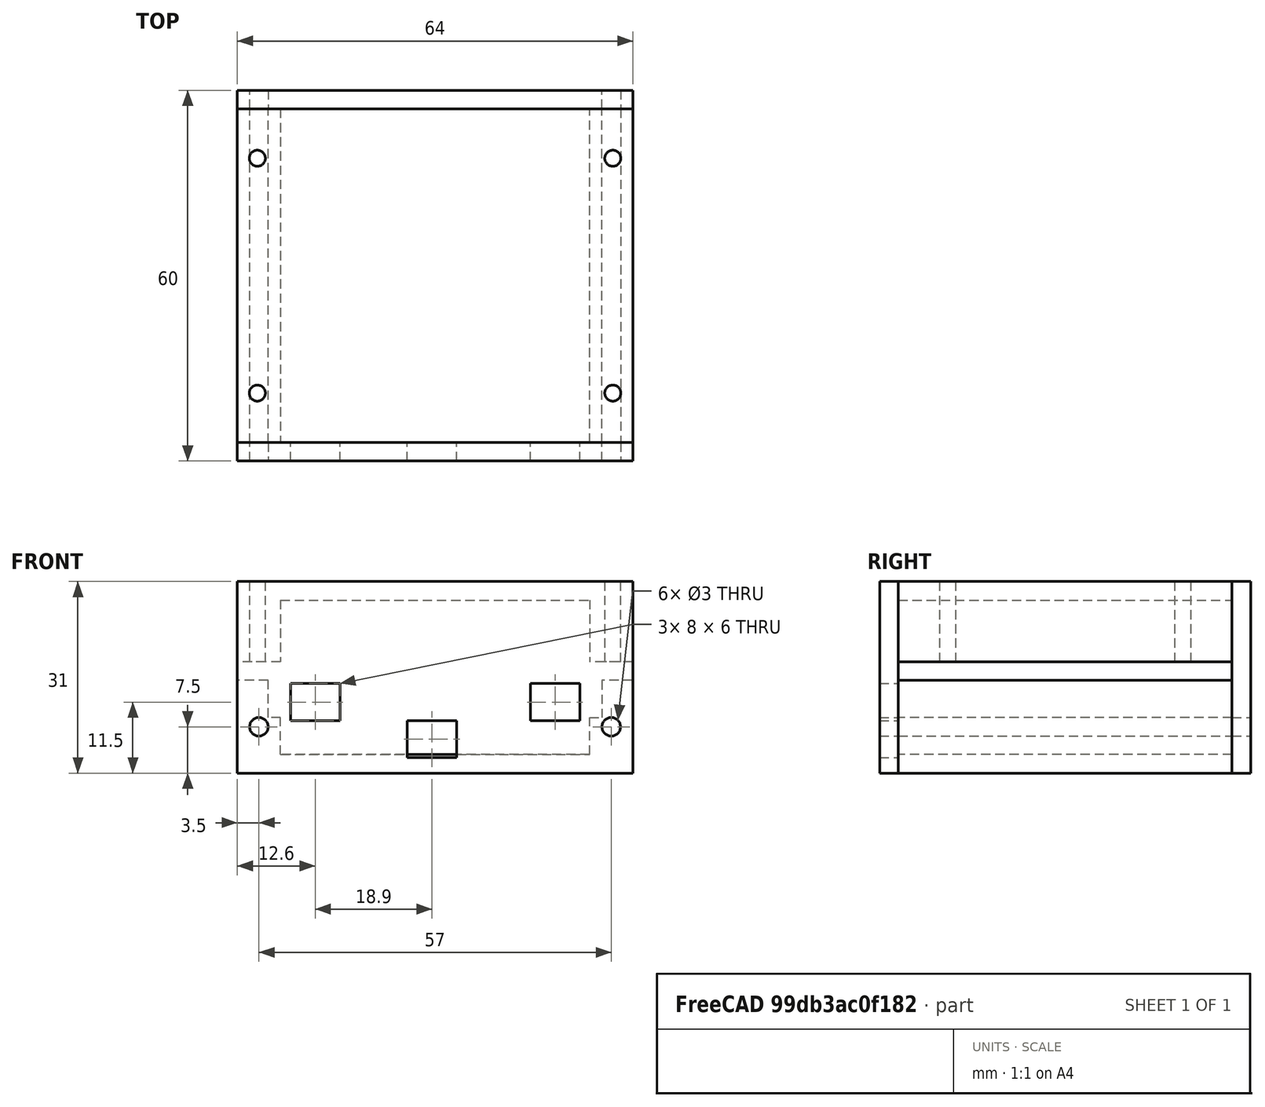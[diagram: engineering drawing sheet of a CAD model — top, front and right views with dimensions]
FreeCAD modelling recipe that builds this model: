
FCSTD DOCUMENT  (FreeCAD 0.20R29603 (Git))
Label: Remote Housing
License: All rights reserved
LicenseURL: http://en.wikipedia.org/wiki/All_rights_reserved
objects: Sketcher::SketchObject×16, PartDesign::Pocket×9, PartDesign::Pad×6, Mesh::Feature×5, PartDesign::Body×4
note: 50 computed .brp shape members not serialized (recipe doc carries the construction recipe); baked Part::Feature solids carry a one-line shape summary decoded from their .brp

FEATURE [Sketcher::SketchObject] Sketch
  FullyConstrained = true
  MapMode = 5
  Support = -> [XY_Plane]
  sketch-geometry (4):
    g0: LineSegment StartX=-32 StartY=27 StartZ=0 EndX=32 EndY=27 EndZ=0
    g1: LineSegment StartX=32 StartY=27 StartZ=0 EndX=32 EndY=-27 EndZ=0
    g2: LineSegment StartX=32 StartY=-27 StartZ=0 EndX=-32 EndY=-27 EndZ=0
    g3: LineSegment StartX=-32 StartY=-27 StartZ=0 EndX=-32 EndY=27 EndZ=0
  constraints (12):
    c: Horizontal(g0)
    c: Vertical(g1)
    c: Horizontal(g2)
    c: Vertical(g3)
    c: Coincident(g3,g0)
    c: Coincident(g0,g1)
    c: Coincident(g2,g1)
    c: Coincident(g2,g3)
    c: DistanceY(g1,g-1) = 27
    c: DistanceX(g-1,g0) = 32
    c: DistanceX(g0,g-1) = 32
    c: DistanceY(g-1,g0) = 27
FEATURE [Mesh::Feature] Holder
FEATURE [PartDesign::Pad] Pad
  Direction = (0,0,1)
  Length = 3
  Length2 = 10
  Profile = -> Sketch
  ReferenceAxis = -> Sketch [N_Axis]
  Type = 0
FEATURE [Mesh::Feature] Unnamed_Goouuu_ESP32_Development_Board001  label="ESP32_Development_Board"
  Placement = pos=(-3.3e-15,12,-3) rot=(-0.57735,-0.57735,0.57735;2.0944rad)
FEATURE [Mesh::Feature] Switch
  Placement = pos=(-10,-21,-9) rot=(0,0,1;3.14159rad)
FEATURE [Mesh::Feature] Switch001
  Placement = pos=(10,-21,-2.5) rot=(0,0,1;3.14159rad)
FEATURE [Mesh::Feature] Switch002
  Placement = pos=(-11,-21,-9) rot=(1,0,0;3.14159rad)
FEATURE [Sketcher::SketchObject] Sketch001  label="ThickWalls"
  FullyConstrained = true
  MapMode = 5
  Placement = pos=(0,0,0) rot=(1,0,0;3.14159rad)
  Support = -> [Pad]
  sketch-geometry (8):
    g0: LineSegment StartX=25 StartY=27 StartZ=0 EndX=32 EndY=27 EndZ=0
    g1: LineSegment StartX=32 StartY=27 StartZ=0 EndX=32 EndY=-27 EndZ=0
    g2: LineSegment StartX=32 StartY=-27 StartZ=0 EndX=25 EndY=-27 EndZ=0
    g3: LineSegment StartX=25 StartY=-27 StartZ=0 EndX=25 EndY=27 EndZ=0
    g4: LineSegment StartX=-32 StartY=27 StartZ=0 EndX=-25 EndY=27 EndZ=0
    g5: LineSegment StartX=-25 StartY=27 StartZ=0 EndX=-25 EndY=-27 EndZ=0
    g6: LineSegment StartX=-25 StartY=-27 StartZ=0 EndX=-32 EndY=-27 EndZ=0
    g7: LineSegment StartX=-32 StartY=-27 StartZ=0 EndX=-32 EndY=27 EndZ=0
  constraints (25):
    c: Horizontal(g0)
    c: Vertical(g1)
    c: Horizontal(g2)
    c: Vertical(g3)
    c: Coincident(g0,g3)
    c: Coincident(g0,g1)
    c: Coincident(g1,g2)
    c: Coincident(g2,g3)
    c: DistanceY(g-1,g0) = 27
    c: DistanceY(g1,g-1) = 27
    c: DistanceX(g-1,g0) = 25
    c: DistanceX(g0,g0) = 7
    c: Horizontal(g4)
    c: Vertical(g5)
    c: Horizontal(g6)
    c: PointOnObject(g7,g6)
    c: Vertical(g7)
    c: Coincident(g4,g7)
    c: Coincident(g4,g5)
    c: Coincident(g5,g6)
    c: DistanceX(g4,g-1) = 25
    c: DistanceX(g4,g4) = 7
    c: DistanceY(g-1,g4) = 27
    c: DistanceY(g7,g-1) = 27
    c: DistanceX(g6,g-1) = 32
FEATURE [PartDesign::Pad] Pad001
  BaseFeature = -> Pad
  Direction = (0,0,-1)
  Length = 10
  Length2 = 10
  Profile = -> Sketch001
  ReferenceAxis = -> Sketch001 [N_Axis]
  Type = 0
FEATURE [Sketcher::SketchObject] Sketch002  label="LeftHoles"
  FullyConstrained = true
  MapMode = 5
  Placement = pos=(0,0,-10) rot=(1,0,0;3.14159rad)
  Support = -> [Pad001]
  sketch-geometry (2):
    g0: Circle CenterX=-28.75 CenterY=19 CenterZ=0 NormalX=0 NormalY=0 NormalZ=1 AngleXU=0 Radius=1.3
    g1: Circle CenterX=-28.75 CenterY=-19 CenterZ=0 NormalX=0 NormalY=0 NormalZ=1 AngleXU=0 Radius=1.3
  constraints (6):
    c: DistanceY(g-1,g0) = 19
    c: DistanceY(g1,g-1) = 19
    c: Diameter(g0) = 2.6
    c: Diameter(g1) = 2.6
    c: DistanceX(g0,g-1) = 28.75
    c: DistanceX(g1,g-1) = 28.75
FEATURE [PartDesign::Pocket] Pocket
  BaseFeature = -> Pad001
  Direction = (0,0,1)
  Length = 20
  Length2 = 5
  Profile = -> Sketch002
  ReferenceAxis = -> Sketch002 [N_Axis]
  Type = 0
FEATURE [Sketcher::SketchObject] Sketch003  label="Right Holes"
  FullyConstrained = true
  MapMode = 5
  Placement = pos=(0,0,-10) rot=(1,0,0;3.14159rad)
  Support = -> [Pocket]
  sketch-geometry (2):
    g0: Circle CenterX=28.75 CenterY=19 CenterZ=0 NormalX=0 NormalY=0 NormalZ=1 AngleXU=0 Radius=1.3
    g1: Circle CenterX=28.75 CenterY=-19 CenterZ=0 NormalX=0 NormalY=0 NormalZ=1 AngleXU=0 Radius=1.3
  constraints (6):
    c: DistanceY(g-1,g0) = 19
    c: DistanceX(g-1,g0) = 28.75
    c: Diameter(g0) = 2.6
    c: DistanceX(g-1,g1) = 28.75
    c: DistanceY(g1,g-1) = 19
    c: Diameter(g1) = 2.6
FEATURE [PartDesign::Pocket] Pocket001
  BaseFeature = -> Pocket
  Direction = (0,0,1)
  Length = 20
  Length2 = 5
  Profile = -> Sketch003
  ReferenceAxis = -> Sketch003 [N_Axis]
  Type = 0
FEATURE [PartDesign::Body] Body  label="Battery Cover Bottom"
  Group = -> [Sketch,Pad,Sketch001,Pad001,Sketch002,Pocket,Sketch003,Pocket001]
  Origin = -> Origin
  Placement = pos=(0,0,10.5) rot=(0,0,1;0rad)
  Tip = -> Pocket001
FEATURE [Sketcher::SketchObject] Sketch004
  FullyConstrained = true
  MapMode = 5
  Support = -> [XY_Plane001]
  sketch-geometry (4):
    g0: LineSegment StartX=-32 StartY=27 StartZ=0 EndX=32 EndY=27 EndZ=0
    g1: LineSegment StartX=32 StartY=27 StartZ=0 EndX=32 EndY=-27 EndZ=0
    g2: LineSegment StartX=32 StartY=-27 StartZ=0 EndX=-32 EndY=-27 EndZ=0
    g3: LineSegment StartX=-32 StartY=-27 StartZ=0 EndX=-32 EndY=27 EndZ=0
  constraints (12):
    c: Horizontal(g0)
    c: Vertical(g1)
    c: Horizontal(g2)
    c: Vertical(g3)
    c: Coincident(g3,g0)
    c: Coincident(g0,g1)
    c: Coincident(g2,g1)
    c: Coincident(g2,g3)
    c: DistanceY(g1,g-1) = 27
    c: DistanceX(g-1,g0) = 32
    c: DistanceX(g0,g-1) = 32
    c: DistanceY(g-1,g0) = 27
FEATURE [PartDesign::Pad] Pad002
  Direction = (0,0,1)
  Length = 3
  Length2 = 10
  Profile = -> Sketch004
  ReferenceAxis = -> Sketch004 [N_Axis]
  Type = 0
FEATURE [Sketcher::SketchObject] Sketch005  label="ThickWalls001"
  FullyConstrained = true
  MapMode = 5
  Placement = pos=(0,0,0) rot=(1,0,0;3.14159rad)
  Support = -> [Pad002]
  sketch-geometry (8):
    g0: LineSegment StartX=25 StartY=27 StartZ=0 EndX=32 EndY=27 EndZ=0
    g1: LineSegment StartX=32 StartY=27 StartZ=0 EndX=32 EndY=-27 EndZ=0
    g2: LineSegment StartX=32 StartY=-27 StartZ=0 EndX=25 EndY=-27 EndZ=0
    g3: LineSegment StartX=25 StartY=-27 StartZ=0 EndX=25 EndY=27 EndZ=0
    g4: LineSegment StartX=-32 StartY=27 StartZ=0 EndX=-25 EndY=27 EndZ=0
    g5: LineSegment StartX=-25 StartY=27 StartZ=0 EndX=-25 EndY=-27 EndZ=0
    g6: LineSegment StartX=-25 StartY=-27 StartZ=0 EndX=-32 EndY=-27 EndZ=0
    g7: LineSegment StartX=-32 StartY=-27 StartZ=0 EndX=-32 EndY=27 EndZ=0
  constraints (25):
    c: Horizontal(g0)
    c: Vertical(g1)
    c: Horizontal(g2)
    c: Vertical(g3)
    c: Coincident(g0,g3)
    c: Coincident(g0,g1)
    c: Coincident(g1,g2)
    c: Coincident(g2,g3)
    c: DistanceY(g-1,g0) = 27
    c: DistanceY(g1,g-1) = 27
    c: DistanceX(g-1,g0) = 25
    c: DistanceX(g0,g0) = 7
    c: Horizontal(g4)
    c: Vertical(g5)
    c: Horizontal(g6)
    c: PointOnObject(g7,g6)
    c: Vertical(g7)
    c: Coincident(g4,g7)
    c: Coincident(g4,g5)
    c: Coincident(g5,g6)
    c: DistanceX(g4,g-1) = 25
    c: DistanceX(g4,g4) = 7
    c: DistanceY(g-1,g4) = 27
    c: DistanceY(g7,g-1) = 27
    c: DistanceX(g6,g-1) = 32
FEATURE [PartDesign::Pad] Pad003
  BaseFeature = -> Pad002
  Direction = (0,0,-1)
  Length = 12
  Length2 = 10
  Profile = -> Sketch005
  ReferenceAxis = -> Sketch005 [N_Axis]
  Type = 0
FEATURE [Sketcher::SketchObject] Sketch008  label="Right"
  FullyConstrained = true
  MapMode = 5
  Placement = pos=(0,-27,0) rot=(1,0,0;1.5708rad)
  Support = -> [Pad003]
  sketch-geometry (1):
    g0: Circle CenterX=28.5 CenterY=-4.5 CenterZ=0 NormalX=0 NormalY=0 NormalZ=1 AngleXU=0 Radius=1.5
  constraints (3):
    c: DistanceX(g-1,g0) = 28.5
    c: Diameter(g0) = 3
    c: DistanceY(g0,g-1) = 4.5
FEATURE [PartDesign::Pocket] Pocket003
  BaseFeature = -> Pad003
  Direction = (0,1,-2e-16)
  Length = 60
  Length2 = 5
  Profile = -> Sketch008
  ReferenceAxis = -> Sketch008 [N_Axis]
  Type = 0
FEATURE [Sketcher::SketchObject] Sketch009  label="Left"
  FullyConstrained = true
  MapMode = 5
  Placement = pos=(0,-27,0) rot=(1,0,0;1.5708rad)
  Support = -> [Pocket003]
  sketch-geometry (1):
    g0: Circle CenterX=-28.5 CenterY=-4.5 CenterZ=0 NormalX=0 NormalY=0 NormalZ=1 AngleXU=0 Radius=1.5
  constraints (3):
    c: Diameter(g0) = 3
    c: DistanceY(g0,g-1) = 4.5
    c: DistanceX(g0,g-1) = 28.5
FEATURE [PartDesign::Pocket] Pocket004
  BaseFeature = -> Pocket003
  Direction = (0,1,-2e-16)
  Length = 60
  Length2 = 5
  Profile = -> Sketch009
  ReferenceAxis = -> Sketch009 [N_Axis]
  Type = 0
FEATURE [Sketcher::SketchObject] Sketch010  label="Side 01"
  FullyConstrained = true
  Placement = pos=(0,30,0) rot=(1,0,0;1.5708rad)
  sketch-geometry (4):
    g0: LineSegment StartX=-32 StartY=13.5 StartZ=0 EndX=32 EndY=13.5 EndZ=0
    g1: LineSegment StartX=32 StartY=13.5 StartZ=0 EndX=32 EndY=-17.5 EndZ=0
    g2: LineSegment StartX=32 StartY=-17.5 StartZ=0 EndX=-32 EndY=-17.5 EndZ=0
    g3: LineSegment StartX=-32 StartY=-17.5 StartZ=0 EndX=-32 EndY=13.5 EndZ=0
  constraints (12):
    c: Horizontal(g0)
    c: Vertical(g1)
    c: Horizontal(g2)
    c: Vertical(g3)
    c: Coincident(g3,g0)
    c: Coincident(g1,g0)
    c: Coincident(g2,g1)
    c: Coincident(g2,g3)
    c: DistanceY(g-1,g0) = 13.5
    c: DistanceX(g0,g-1) = 32
    c: DistanceX(g-1,g0) = 32
    c: DistanceY(g2,g-1) = 17.5
FEATURE [PartDesign::Pad] Pad005
  Direction = (0,-1,2e-16)
  Length = 3
  Length2 = 10
  Placement = pos=(0,30,0) rot=(1,0,0;1.5708rad)
  Profile = -> Sketch010
  ReferenceAxis = -> Sketch010 [N_Axis]
  Type = 0
FEATURE [Sketcher::SketchObject] Sketch011  label="SideHoles"
  FullyConstrained = true
  MapMode = 5
  Placement = pos=(0,30,0) rot=(-1,0,0;1.5708rad)
  Support = -> [Pad005]
  sketch-geometry (2):
    g0: Circle CenterX=28.5 CenterY=10 CenterZ=0 NormalX=0 NormalY=0 NormalZ=1 AngleXU=0 Radius=1.5
    g1: Circle CenterX=-28.5 CenterY=10 CenterZ=0 NormalX=0 NormalY=0 NormalZ=1 AngleXU=0 Radius=1.5
  constraints (6):
    c: Diameter(g0) = 3
    c: Diameter(g1) = 3
    c: DistanceY(g-1,g1) = 10
    c: DistanceY(g-1,g0) = 10
    c: DistanceX(g-1,g0) = 28.5
    c: DistanceX(g1,g-1) = 28.5
FEATURE [PartDesign::Pocket] Pocket005
  BaseFeature = -> Pad005
  Direction = (0,-1,2e-16)
  Length = 5
  Length2 = 5
  Placement = pos=(0,30,0) rot=(1,0,0;1.5708rad)
  Profile = -> Sketch011
  ReferenceAxis = -> Sketch011 [N_Axis]
  Type = 0
FEATURE [PartDesign::Body] Body003  label="Side1"
  Group = -> [Sketch010,Pad005,Sketch011,Pocket005]
  Origin = -> Origin003
  Tip = -> Pocket005
FEATURE [Sketcher::SketchObject] Sketch012  label="Side 002"
  FullyConstrained = true
  Placement = pos=(0,30,0) rot=(1,0,0;1.5708rad)
  sketch-geometry (4):
    g0: LineSegment StartX=-32 StartY=13.5 StartZ=0 EndX=32 EndY=13.5 EndZ=0
    g1: LineSegment StartX=32 StartY=13.5 StartZ=0 EndX=32 EndY=-17.5 EndZ=0
    g2: LineSegment StartX=32 StartY=-17.5 StartZ=0 EndX=-32 EndY=-17.5 EndZ=0
    g3: LineSegment StartX=-32 StartY=-17.5 StartZ=0 EndX=-32 EndY=13.5 EndZ=0
  constraints (12):
    c: Horizontal(g0)
    c: Vertical(g1)
    c: Horizontal(g2)
    c: Vertical(g3)
    c: Coincident(g3,g0)
    c: Coincident(g1,g0)
    c: Coincident(g2,g1)
    c: Coincident(g2,g3)
    c: DistanceY(g-1,g0) = 13.5
    c: DistanceX(g0,g-1) = 32
    c: DistanceX(g-1,g0) = 32
    c: DistanceY(g2,g-1) = 17.5
FEATURE [PartDesign::Pad] Pad006
  Direction = (0,-1,2e-16)
  Length = 3
  Length2 = 10
  Placement = pos=(0,30,0) rot=(1,0,0;1.5708rad)
  Profile = -> Sketch012
  ReferenceAxis = -> Sketch012 [N_Axis]
  Type = 0
FEATURE [Sketcher::SketchObject] Sketch013  label="SideHoles001"
  FullyConstrained = true
  MapMode = 5
  Placement = pos=(0,30,0) rot=(-1,0,0;1.5708rad)
  Support = -> [Pad006]
  sketch-geometry (2):
    g0: Circle CenterX=28.5 CenterY=10 CenterZ=0 NormalX=0 NormalY=0 NormalZ=1 AngleXU=0 Radius=1.5
    g1: Circle CenterX=-28.5 CenterY=10 CenterZ=0 NormalX=0 NormalY=0 NormalZ=1 AngleXU=0 Radius=1.5
  constraints (6):
    c: Diameter(g0) = 3
    c: Diameter(g1) = 3
    c: DistanceY(g-1,g1) = 10
    c: DistanceY(g-1,g0) = 10
    c: DistanceX(g-1,g0) = 28.5
    c: DistanceX(g1,g-1) = 28.5
FEATURE [PartDesign::Pocket] Pocket006
  BaseFeature = -> Pad006
  Direction = (0,-1,2e-16)
  Length = 5
  Length2 = 5
  Placement = pos=(0,30,0) rot=(1,0,0;1.5708rad)
  Profile = -> Sketch013
  ReferenceAxis = -> Sketch013 [N_Axis]
  Type = 0
FEATURE [Sketcher::SketchObject] Sketch014  label="SwitchHoles"
  FullyConstrained = true
  MapMode = 5
  Placement = pos=(0,27,1e-15) rot=(1,0,0;1.5708rad)
  Support = -> [Pocket006]
  sketch-geometry (12):
    g0: LineSegment StartX=15.4 StartY=-3 StartZ=0 EndX=23.4 EndY=-3 EndZ=0
    g1: LineSegment StartX=23.4 StartY=-3 StartZ=0 EndX=23.4 EndY=-9 EndZ=0
    g2: LineSegment StartX=23.4 StartY=-9 StartZ=0 EndX=15.4 EndY=-9 EndZ=0
    g3: LineSegment StartX=15.4 StartY=-9 StartZ=0 EndX=15.4 EndY=-3 EndZ=0
    g4: LineSegment StartX=-4.5 StartY=-9 StartZ=0 EndX=3.5 EndY=-9 EndZ=0
    g5: LineSegment StartX=3.5 StartY=-9 StartZ=0 EndX=3.5 EndY=-15 EndZ=0
    g6: LineSegment StartX=3.5 StartY=-15 StartZ=0 EndX=-4.5 EndY=-15 EndZ=0
    g7: LineSegment StartX=-4.5 StartY=-15 StartZ=0 EndX=-4.5 EndY=-9 EndZ=0
    g8: LineSegment StartX=-23.4 StartY=-3 StartZ=0 EndX=-15.4 EndY=-3 EndZ=0
    g9: LineSegment StartX=-15.4 StartY=-3 StartZ=0 EndX=-15.4 EndY=-9 EndZ=0
    g10: LineSegment StartX=-15.4 StartY=-9 StartZ=0 EndX=-23.4 EndY=-9 EndZ=0
    g11: LineSegment StartX=-23.4 StartY=-9 StartZ=0 EndX=-23.4 EndY=-3 EndZ=0
  constraints (36):
    c: Horizontal(g0)
    c: Vertical(g1)
    c: Horizontal(g2)
    c: Vertical(g3)
    c: Coincident(g3,g0)
    c: Coincident(g0,g1)
    c: Coincident(g1,g2)
    c: Coincident(g2,g3)
    c: DistanceX(g-1,g0) = 23.4
    c: DistanceY(g0,g-1) = 3
    c: DistanceX(g2,g1) = 8
    c: DistanceY(g2,g0) = 6
    c: Horizontal(g4)
    c: Vertical(g5)
    c: Horizontal(g6)
    c: Coincident(g4,g7)
    c: Coincident(g6,g7)
    c: Coincident(g6,g5)
    c: Coincident(g5,g4)
    c: DistanceX(g-1,g4) = 3.5
    c: DistanceY(g4,g-1) = 9
    c: DistanceX(g6,g5) = 8
    c: DistanceX(g4,g4) = 8
    c: DistanceY(g6,g4) = 6
    c: Horizontal(g8)
    c: Coincident(g8,g11)
    c: Coincident(g8,g9)
    c: Coincident(g10,g9)
    c: Coincident(g10,g11)
    c: DistanceX(g8,g-1) = 23.4
    c: DistanceY(g8,g-1) = 3
    c: DistanceX(g10,g9) = 8
    c: DistanceY(g9,g9) = 6
    c: DistanceX(g8,g8) = 8
    c: Angle(g11,g8) = 1.5708
    c: Angle(g10,g11) = 1.5708
FEATURE [PartDesign::Pocket] Pocket007
  BaseFeature = -> Pocket006
  Direction = (0,1,-4e-16)
  Length = 5
  Length2 = 5
  Placement = pos=(0,30,0) rot=(1,0,0;1.5708rad)
  Profile = -> Sketch014
  ReferenceAxis = -> Sketch014 [N_Axis]
  Type = 0
FEATURE [Sketcher::SketchObject] Sketch015
  FullyConstrained = true
  MapMode = 5
  Placement = pos=(0,0,0) rot=(1,0,0;1.5708rad)
  Support = -> [XZ_Plane004]
FEATURE [PartDesign::Body] Body004  label="Side002"
  Group = -> [Sketch012,Pad006,Sketch013,Pocket006,Sketch014,Pocket007,Sketch015]
  Origin = -> Origin004
  Placement = pos=(0,-57,0) rot=(0,0,1;0rad)
  Tip = -> Pocket007
FEATURE [Sketcher::SketchObject] Sketch016  label="ESP32 Cutout 1"
  FullyConstrained = true
  MapMode = 5
  Placement = pos=(-25,0,0) rot=(0.57735,0.57735,0.57735;2.0944rad)
  Support = -> [Pocket004]
  sketch-geometry (4):
    g0: LineSegment StartX=-27 StartY=-6 StartZ=0 EndX=27 EndY=-6 EndZ=0
    g1: LineSegment StartX=27 StartY=-6 StartZ=0 EndX=27 EndY=-12 EndZ=0
    g2: LineSegment StartX=27 StartY=-12 StartZ=0 EndX=-27 EndY=-12 EndZ=0
    g3: LineSegment StartX=-27 StartY=-12 StartZ=0 EndX=-27 EndY=-6 EndZ=0
  constraints (12):
    c: Horizontal(g0)
    c: Coincident(g1,g0)
    c: Horizontal(g2)
    c: Coincident(g3,g2)
    c: Coincident(g0,g3)
    c: Coincident(g2,g1)
    c: DistanceX(g0,g-1) = 27
    c: DistanceX(g2,g-1) = 27
    c: DistanceX(g-1,g1) = 27
    c: DistanceX(g-1,g0) = 27
    c: DistanceY(g2,g0) = 6
    c: DistanceY(g0,g-1) = 6
FEATURE [PartDesign::Pocket] Pocket008
  BaseFeature = -> Pocket004
  Direction = (-1,0,0)
  Length = 2
  Length2 = 5
  Profile = -> Sketch016
  ReferenceAxis = -> Sketch016 [N_Axis]
  Type = 0
FEATURE [Sketcher::SketchObject] Sketch017  label="ESP32Cutout2"
  FullyConstrained = true
  MapMode = 5
  Placement = pos=(25,0,0) rot=(0.57735,-0.57735,-0.57735;2.0944rad)
  Support = -> [Pocket008]
  sketch-geometry (4):
    g0: LineSegment StartX=-27 StartY=-6 StartZ=0 EndX=27 EndY=-6 EndZ=0
    g1: LineSegment StartX=27 StartY=-12 StartZ=0 EndX=-27 EndY=-12 EndZ=0
    g2: LineSegment StartX=-27 StartY=-12 StartZ=0 EndX=-27 EndY=-6 EndZ=0
    g3: LineSegment StartX=27 StartY=-6 StartZ=0 EndX=27 EndY=-12 EndZ=0
  constraints (12):
    c: Horizontal(g0)
    c: Horizontal(g1)
    c: Vertical(g2)
    c: Vertical(g3)
    c: Coincident(g0,g3)
    c: Coincident(g1,g3)
    c: Coincident(g1,g2)
    c: Coincident(g0,g2)
    c: DistanceX(g-1,g0) = 27
    c: DistanceX(g0,g-1) = 27
    c: DistanceY(g1,g0) = 6
    c: DistanceY(g0,g-1) = 6
FEATURE [PartDesign::Pocket] Pocket009
  BaseFeature = -> Pocket008
  Direction = (1,0,0)
  Length = 2
  Length2 = 5
  Profile = -> Sketch017
  ReferenceAxis = -> Sketch017 [N_Axis]
  Type = 0
FEATURE [PartDesign::Body] Body001  label="Battery Cover Top"
  Group = -> [Sketch004,Pad002,Sketch005,Pad003,Sketch008,Pocket003,Sketch009,Pocket004,Sketch016,Pocket008,Sketch017,Pocket009]
  Origin = -> Origin001
  Placement = pos=(0,-3e-15,-14.5) rot=(1,0,0;3.14159rad)
  Tip = -> Pocket009
